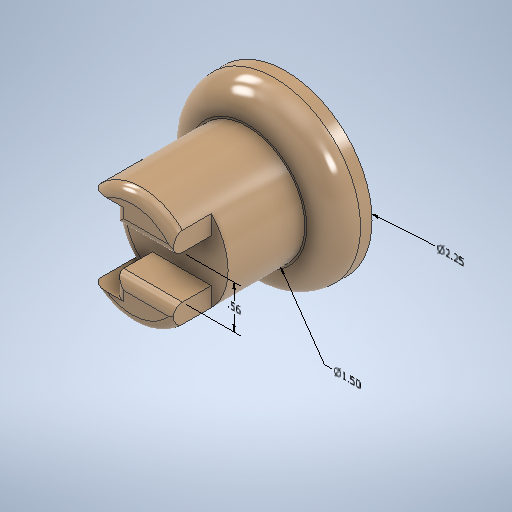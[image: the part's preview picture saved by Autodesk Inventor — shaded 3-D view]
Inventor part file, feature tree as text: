
AUTODESK INVENTOR PART (.ipt)
format: ipt  version: 2025.2 (Build 292293000, 293)  size: 392,192 bytes
history: native  units: in
note: dims shown in document units (in); Inventor stores cm internally (conversion verified against a paired STEP export)
features: extrude x8, sketch x8, other x4, fillet x3
ambient origin geometry x8: Origin, YZ Plane, XZ Plane, XY Plane, X Axis, Y Axis, Z Axis, Center Point
bodies: Solid1 (feature_tree)
feature tree (23):
  other  "Annotations"
  extrude  "Extrusion1"  Depth=0.5in TaperAngle=0.0deg
  extrude  "Extrusion2"  Depth=0.25in TaperAngle=0.0deg
  extrude  "Extrusion3"  Depth=0.25in TaperAngle=0.0deg
  sketch  "Sketch4"  dims[d9=1.5in d10=0.25in d11=0.0in]
  sketch  "Sketch5"  dims[d12=1.0in d13=0.0in d17=0.5in d18=0.0in]
  extrude  "Extrusion4"  Depth=0.25in TaperAngle=0.0deg
  extrude  "Extrusion5"  Depth=0.5in TaperAngle=0.0deg
  extrude  "Extrusion6"  Depth=0.25in TaperAngle=0.0deg
  fillet  "Fillet1"  Radius=0.25in
  extrude  "Extrusion7"  Depth=0.125in
  extrude  "Extrusion8"  [1 undecoded]
  fillet  "Fillet2"  [1 undecoded]
  fillet  "Fillet3"  [1 undecoded]
  sketch  "Sketch1"  dims[d0=2.25in d1=0.5in d2=0.0in]
  sketch  "Sketch2"  dims[d3=1.8in d4=0.25in d5=0.0in]
  sketch  "Sketch3"  dims[d6=0.85in d7=0.25in d8=0.0in]
  sketch  "Sketch6"  dims[d19=0.17in d20=0.25in d21=0.0in d22=0.25in d23=0.0in]
  sketch  "Sketch7"  dims[d24=0.35in d25=0.125in]
  sketch  "Sketch8"  dims[d26=0.2651in d27=0.191in d28=0.5612in d29=1.2112in d30=2.25in d31=2.096in d32=1.5in]
  other  "Linear Dimension 1"
  other  "Diameter Dimension 1"
  other  "Diameter Dimension 2"
note: 3 required parameter values undecoded (feature->parameter linkage not recoverable at this tier; creation-order binding heuristic only, values carry confidence <= 0.55)
